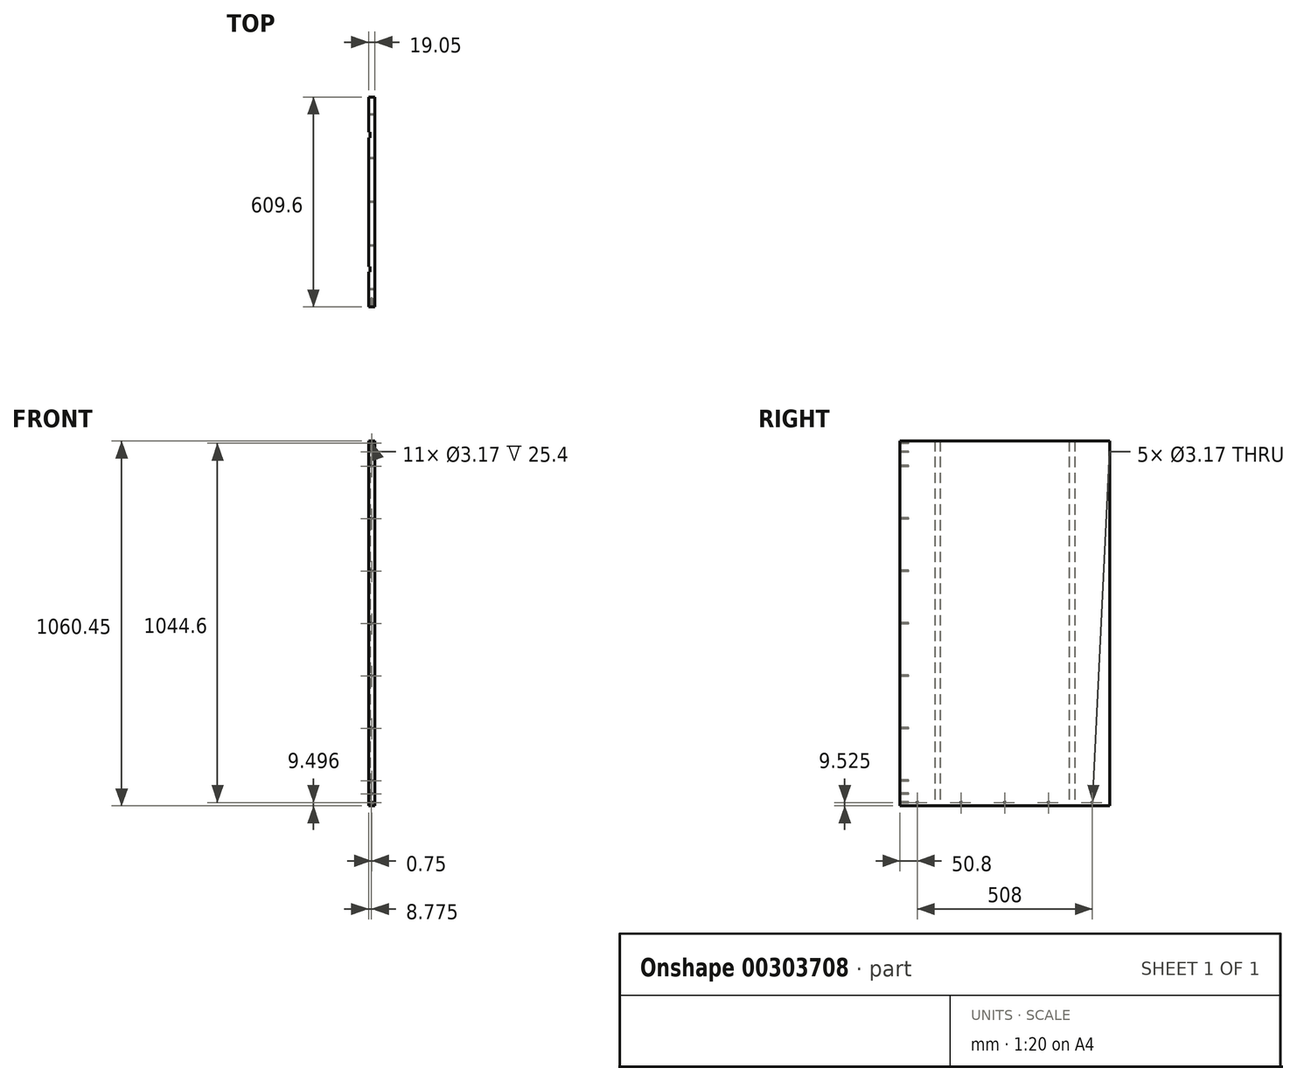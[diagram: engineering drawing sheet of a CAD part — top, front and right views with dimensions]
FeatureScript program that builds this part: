
annotation { "Feature Type Name" : "Feature", "Feature Type Description" : "" }
export const myFeature = defineFeature(function(context is Context, id is Id, definition is map)
    precondition{}
    {
        {
            var Q0;
            Q0=qCreatedBy(makeId("Front.planeOp"),FACE);
            var sketch = newSketch(context, id + "F0", { "sketchPlane" : qUnion([Q0])});
            skLineSegment(sketch, "E0.bottom", {"start": v(0, 0) * mm, "end": v(19.05, 0) * mm});
            skLineSegment(sketch, "E0.top", {"start": v(0, 1060.45) * mm, "end": v(19.05, 1060.45) * mm});
            skLineSegment(sketch, "E0.left", {"start": v(0, 0) * mm, "end": v(0, 1060.45) * mm});
            skLineSegment(sketch, "E0.right", {"start": v(19.05, 0) * mm, "end": v(19.05, 1060.45) * mm});
            skSolve(sketch);
        }
        {
            var Q0;
            Q0 = qSketchRegion(id + "F0", true);
            extrude(context, id + "F1", {"entities" : qUnion([Q0]), "oppositeDirection" : true, "depth" : 609.6 * mm});
        }
        {
            var Q0;
            Q0=qCreatedBy(makeId("Right.planeOp"),FACE);
            var sketch = newSketch(context, id + "F2", { "sketchPlane" : qUnion([Q0])});
            skCircle(sketch, "E1", {"center": v(50.8, 9.53) * mm, "radius": 1.59 * mm});
            skCircle(sketch, "E2.1.0.0", {"center": v(177.8, 9.53) * mm, "radius": 1.59 * mm});
            skCircle(sketch, "E2.2.0.0", {"center": v(304.8, 9.53) * mm, "radius": 1.59 * mm});
            skCircle(sketch, "E2.3.0.0", {"center": v(431.8, 9.53) * mm, "radius": 1.59 * mm});
            skCircle(sketch, "E2.4.0.0", {"center": v(558.8, 9.53) * mm, "radius": 1.59 * mm});
            skLineSegment(sketch, "E2.direction1", {"start": v(50.8, 9.53) * mm, "end": v(177.8, 9.53) * mm, "construction": true});
            skSolve(sketch);
        }
        {
            var Q0;
            Q0 = qSketchRegion(id + "F2", true);
            extrude(context, id + "F3", {"entities" : qUnion([Q0]), "operationType" : NewBodyOperationType.REMOVE, "endBound" : BoundingType.THROUGH_ALL, "depth" : 25.4 * mm});
        }
        {
            var Q0;
            Q0=qCreatedBy(makeId("Front.planeOp"),FACE);
            var sketch = newSketch(context, id + "F4", { "sketchPlane" : qUnion([Q0])});
            skCircle(sketch, "E3", {"center": v(9.52, 1054.1) * mm, "radius": 1.59 * mm});
            skCircle(sketch, "E4.1.0.0", {"center": v(9.4, 1028.7) * mm, "radius": 1.59 * mm});
            skLineSegment(sketch, "E4.direction1", {"start": v(9.52, 1054.1) * mm, "end": v(9.4, 1028.7) * mm, "construction": true});
            skSolve(sketch);
        }
        {
            var Q0;
            Q0 = qSketchRegion(id + "F4", true);
            extrude(context, id + "F5", {"entities" : qUnion([Q0]), "operationType" : NewBodyOperationType.REMOVE, "oppositeDirection" : true, "depth" : 25.4 * mm});
        }
        {
            var Q0;
            Q0=qCreatedBy(makeId("Front.planeOp"),FACE);
            var sketch = newSketch(context, id + "F6", { "sketchPlane" : qUnion([Q0])});
            skCircle(sketch, "E5", {"center": v(8.77, 9.5) * mm, "radius": 1.59 * mm});
            skCircle(sketch, "E6.0.1.0", {"center": v(8.77, 34.9) * mm, "radius": 1.59 * mm});
            skLineSegment(sketch, "E6.direction1", {"start": v(8.77, 9.5) * mm, "end": v(8.9, 9.65) * mm, "construction": true});
            skLineSegment(sketch, "E6.direction2", {"start": v(8.77, 9.5) * mm, "end": v(8.77, 34.9) * mm, "construction": true});
            skSolve(sketch);
        }
        {
            var Q0;
            Q0 = qSketchRegion(id + "F6", true);
            extrude(context, id + "F7", {"entities" : qUnion([Q0]), "operationType" : NewBodyOperationType.REMOVE, "oppositeDirection" : true, "depth" : 25.4 * mm});
        }
        {
            var Q0;
            Q0=qCreatedBy(makeId("Front.planeOp"),FACE);
            var sketch = newSketch(context, id + "F8", { "sketchPlane" : qUnion([Q0])});
            skCircle(sketch, "E7", {"center": v(9.53, 987.43) * mm, "radius": 1.59 * mm});
            skCircle(sketch, "E8.0.1.0", {"center": v(9.53, 835.03) * mm, "radius": 1.59 * mm});
            skCircle(sketch, "E8.0.2.0", {"center": v(9.53, 682.63) * mm, "radius": 1.59 * mm});
            skCircle(sketch, "E8.0.3.0", {"center": v(9.53, 530.23) * mm, "radius": 1.59 * mm});
            skCircle(sketch, "E8.0.4.0", {"center": v(9.53, 377.83) * mm, "radius": 1.59 * mm});
            skCircle(sketch, "E8.0.5.0", {"center": v(9.53, 225.43) * mm, "radius": 1.59 * mm});
            skCircle(sketch, "E8.0.6.0", {"center": v(9.53, 73.03) * mm, "radius": 1.59 * mm});
            skLineSegment(sketch, "E8.direction1", {"start": v(9.53, 987.43) * mm, "end": v(34.92, 987.43) * mm, "construction": true});
            skLineSegment(sketch, "E8.direction2", {"start": v(9.53, 987.43) * mm, "end": v(9.53, 835.03) * mm, "construction": true});
            skSolve(sketch);
        }
        {
            var Q0;
            Q0 = qSketchRegion(id + "F8", true);
            extrude(context, id + "F9", {"entities" : qUnion([Q0]), "operationType" : NewBodyOperationType.REMOVE, "oppositeDirection" : true, "depth" : 25.4 * mm});
        }
        {
            var Q0;
            Q0=qCreatedBy(makeId("Top.planeOp"),FACE);
            var sketch = newSketch(context, id + "F10", { "sketchPlane" : qUnion([Q0])});
            skLineSegment(sketch, "E9.bottom", {"start": v(4.83, 101.6) * mm, "end": v(0, 101.6) * mm});
            skLineSegment(sketch, "E9.top", {"start": v(4.83, 117.48) * mm, "end": v(0, 117.48) * mm});
            skLineSegment(sketch, "E9.left", {"start": v(4.83, 101.6) * mm, "end": v(4.83, 117.48) * mm});
            skLineSegment(sketch, "E9.right", {"start": v(0, 101.6) * mm, "end": v(0, 117.48) * mm});
            skSolve(sketch);
        }
        {
            var Q0;
            Q0 = qSketchRegion(id + "F10", true);
            extrude(context, id + "F11", {"entities" : qUnion([Q0]), "operationType" : NewBodyOperationType.REMOVE, "endBound" : BoundingType.THROUGH_ALL, "depth" : 25.4 * mm, "offsetDistance" : 25.4 * mm});
        }
        {
            var Q0;
            Q0=qCreatedBy(makeId("Top.planeOp"),FACE);
            var sketch = newSketch(context, id + "F12", { "sketchPlane" : qUnion([Q0])});
            skLineSegment(sketch, "E10.bottom", {"start": v(0, 508) * mm, "end": v(4.83, 508) * mm});
            skLineSegment(sketch, "E10.top", {"start": v(0, 492.13) * mm, "end": v(4.83, 492.13) * mm});
            skLineSegment(sketch, "E10.left", {"start": v(0, 508) * mm, "end": v(0, 492.13) * mm});
            skLineSegment(sketch, "E10.right", {"start": v(4.83, 508) * mm, "end": v(4.83, 492.13) * mm});
            skSolve(sketch);
        }
        {
            var Q0;
            Q0 = qSketchRegion(id + "F12", true);
            extrude(context, id + "F13", {"entities" : qUnion([Q0]), "operationType" : NewBodyOperationType.REMOVE, "endBound" : BoundingType.THROUGH_ALL, "depth" : 25.4 * mm, "offsetDistance" : 25.4 * mm});
        }
    });
